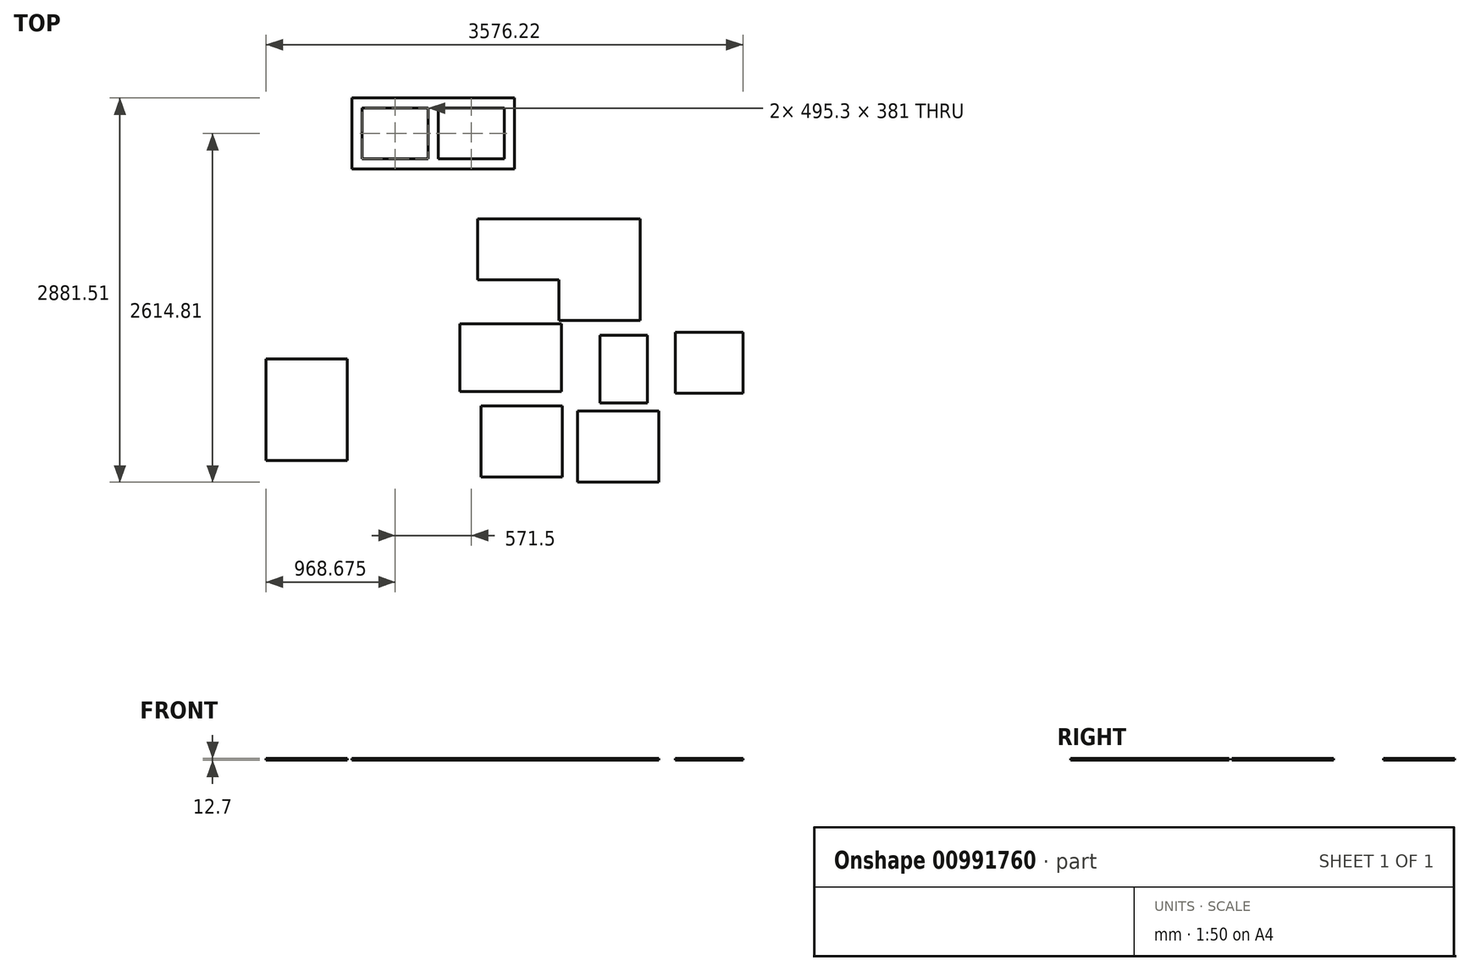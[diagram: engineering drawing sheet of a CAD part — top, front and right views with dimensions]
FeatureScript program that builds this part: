
annotation { "Feature Type Name" : "Feature", "Feature Type Description" : "" }
export const myFeature = defineFeature(function(context is Context, id is Id, definition is map)
    precondition{}
    {
        {
            var Q0;
            Q0=qCreatedBy(makeId("Top.planeOp"),FACE);
            var sketch = newSketch(context, id + "F0", { "sketchPlane" : qUnion([Q0])});
            skLineSegment(sketch, "E0.bottom", {"start": v(-682.65, 340.86) * mm, "end": v(536.55, 340.86) * mm});
            skLineSegment(sketch, "E0.top", {"start": v(-73.05, -421.14) * mm, "end": v(536.55, -421.14) * mm});
            skLineSegment(sketch, "E0.left", {"start": v(-682.65, 340.86) * mm, "end": v(-682.65, -116.34) * mm});
            skLineSegment(sketch, "E0.right", {"start": v(536.55, 340.86) * mm, "end": v(536.55, -421.14) * mm});
            skLineSegment(sketch, "E1", {"start": v(-682.65, -116.34) * mm, "end": v(-73.05, -116.34) * mm});
            skLineSegment(sketch, "E2", {"start": v(-73.05, -116.34) * mm, "end": v(-73.05, -421.14) * mm});
            skLineSegment(sketch, "E3.bottom", {"start": v(-815.3, -443.71) * mm, "end": v(-53.3, -443.71) * mm});
            skLineSegment(sketch, "E3.top", {"start": v(-815.3, -951.71) * mm, "end": v(-53.3, -951.71) * mm});
            skLineSegment(sketch, "E3.left", {"start": v(-815.3, -443.71) * mm, "end": v(-815.3, -951.71) * mm});
            skLineSegment(sketch, "E3.right", {"start": v(-53.3, -443.71) * mm, "end": v(-53.3, -951.71) * mm});
            skLineSegment(sketch, "E4.bottom", {"start": v(234.97, -530.08) * mm, "end": v(590.57, -530.08) * mm});
            skLineSegment(sketch, "E4.top", {"start": v(234.97, -1038.08) * mm, "end": v(590.57, -1038.08) * mm});
            skLineSegment(sketch, "E4.left", {"start": v(234.97, -530.08) * mm, "end": v(234.97, -1038.08) * mm});
            skLineSegment(sketch, "E4.right", {"start": v(590.57, -530.08) * mm, "end": v(590.57, -1038.08) * mm});
            skLineSegment(sketch, "E5.bottom", {"start": v(-656.38, -1060.91) * mm, "end": v(-46.78, -1060.91) * mm});
            skLineSegment(sketch, "E5.top", {"start": v(-656.38, -1594.31) * mm, "end": v(-46.78, -1594.31) * mm});
            skLineSegment(sketch, "E5.left", {"start": v(-656.38, -1060.91) * mm, "end": v(-656.38, -1594.31) * mm});
            skLineSegment(sketch, "E5.right", {"start": v(-46.78, -1060.91) * mm, "end": v(-46.78, -1594.31) * mm});
            skLineSegment(sketch, "E6.bottom", {"start": v(65.68, -1098.92) * mm, "end": v(675.28, -1098.92) * mm});
            skLineSegment(sketch, "E6.top", {"start": v(65.68, -1632.32) * mm, "end": v(675.28, -1632.32) * mm});
            skLineSegment(sketch, "E6.left", {"start": v(65.68, -1098.92) * mm, "end": v(65.68, -1632.32) * mm});
            skLineSegment(sketch, "E6.right", {"start": v(675.28, -1098.92) * mm, "end": v(675.28, -1632.32) * mm});
            skLineSegment(sketch, "E7.bottom", {"start": v(798.33, -507.17) * mm, "end": v(1306.33, -507.17) * mm});
            skLineSegment(sketch, "E7.top", {"start": v(798.33, -964.37) * mm, "end": v(1306.33, -964.37) * mm});
            skLineSegment(sketch, "E7.left", {"start": v(798.33, -507.17) * mm, "end": v(798.33, -964.37) * mm});
            skLineSegment(sketch, "E7.right", {"start": v(1306.33, -507.17) * mm, "end": v(1306.33, -964.37) * mm});
            skLineSegment(sketch, "E8.bottom", {"start": v(-2269.89, -710.02) * mm, "end": v(-1660.29, -710.02) * mm});
            skLineSegment(sketch, "E8.top", {"start": v(-2269.89, -1472.02) * mm, "end": v(-1660.29, -1472.02) * mm});
            skLineSegment(sketch, "E8.left", {"start": v(-2269.89, -710.02) * mm, "end": v(-2269.89, -1472.02) * mm});
            skLineSegment(sketch, "E8.right", {"start": v(-1660.29, -710.02) * mm, "end": v(-1660.29, -1472.02) * mm});
            skText(sketch, "E9", { "text": "X2", "fontName": "OpenSans-Regular.ttf"});
            skLineSegment(sketch, "E10.bottom", {"start": v(-1625.06, 1249.19) * mm, "end": v(-405.86, 1249.19) * mm});
            skLineSegment(sketch, "E10.top", {"start": v(-1625.06, 715.79) * mm, "end": v(-405.86, 715.79) * mm});
            skLineSegment(sketch, "E10.left", {"start": v(-1625.06, 1249.19) * mm, "end": v(-1625.06, 715.79) * mm});
            skLineSegment(sketch, "E10.right", {"start": v(-405.86, 1249.19) * mm, "end": v(-405.86, 715.79) * mm});
            skLineSegment(sketch, "E11.bottom", {"start": v(-1548.86, 1172.99) * mm, "end": v(-1053.56, 1172.99) * mm});
            skLineSegment(sketch, "E11.top", {"start": v(-1548.86, 791.99) * mm, "end": v(-1053.56, 791.99) * mm});
            skLineSegment(sketch, "E11.left", {"start": v(-1548.86, 1172.99) * mm, "end": v(-1548.86, 791.99) * mm});
            skLineSegment(sketch, "E11.right", {"start": v(-482.06, 1172.99) * mm, "end": v(-482.06, 791.99) * mm});
            skLineSegment(sketch, "E12", {"start": v(-1015.46, 1249.19) * mm, "end": v(-1015.46, 640.4) * mm, "construction": true});
            skLineSegment(sketch, "E13", {"start": v(-1053.56, 1172.99) * mm, "end": v(-1053.56, 791.99) * mm});
            skLineSegment(sketch, "E14", {"start": v(-977.36, 1172.99) * mm, "end": v(-977.36, 791.99) * mm});
            skLineSegment(sketch, "E15.trimOffspring", {"start": v(-977.36, 1172.99) * mm, "end": v(-482.06, 1172.99) * mm});
            skLineSegment(sketch, "E16.trimOffspring", {"start": v(-977.36, 791.99) * mm, "end": v(-482.06, 791.99) * mm});
            const initialGuessF0  = {"E9": [0.90316, 0.09607, 1, 0, 0.20292]};
            skSetInitialGuess(sketch, initialGuessF0);
            skSolve(sketch);
        }
        {
            var Q0;
            Q0=makeQuery(id+"F0.imprint","IMPRINT",FACE,{"disambiguationData":[TD([[makeQuery(id+"F0.imprint","IMPRINT",EDGE,{"derivedFrom":sQuery(id+"F0.wireOp",EDGE,"E0.bottom")}),-1.0]])]});
            var Q1;
            Q1=makeQuery(id+"F0.imprint","IMPRINT",FACE,{"disambiguationData":[TD([[makeQuery(id+"F0.imprint","IMPRINT",EDGE,{"derivedFrom":sQuery(id+"F0.wireOp",EDGE,"E3.bottom")}),-1.0]])]});
            var Q2;
            Q2=makeQuery(id+"F0.imprint","IMPRINT",FACE,{"disambiguationData":[TD([[makeQuery(id+"F0.imprint","IMPRINT",EDGE,{"derivedFrom":sQuery(id+"F0.wireOp",EDGE,"E5.bottom")}),-1.0]])]});
            var Q3;
            Q3=makeQuery(id+"F0.imprint","IMPRINT",FACE,{"disambiguationData":[TD([[makeQuery(id+"F0.imprint","IMPRINT",EDGE,{"derivedFrom":sQuery(id+"F0.wireOp",EDGE,"E6.bottom")}),-1.0]])]});
            var Q4;
            Q4=makeQuery(id+"F0.imprint","IMPRINT",FACE,{"disambiguationData":[TD([[makeQuery(id+"F0.imprint","IMPRINT",EDGE,{"derivedFrom":sQuery(id+"F0.wireOp",EDGE,"E4.bottom")}),-1.0]])]});
            var Q5;
            Q5=makeQuery(id+"F0.imprint","IMPRINT",FACE,{"disambiguationData":[TD([[makeQuery(id+"F0.imprint","IMPRINT",EDGE,{"derivedFrom":sQuery(id+"F0.wireOp",EDGE,"E7.bottom")}),-1.0]])]});
            var Q6;
            Q6=makeQuery(id+"F0.imprint","IMPRINT",FACE,{"disambiguationData":[TD([[makeQuery(id+"F0.imprint","IMPRINT",EDGE,{"derivedFrom":sQuery(id+"F0.wireOp",EDGE,"E8.bottom")}),-1.0]])]});
            var Q7;
            Q7=makeQuery(id+"F0.imprint","IMPRINT",FACE,{"disambiguationData":[TD([[makeQuery(id+"F0.imprint","IMPRINT",EDGE,{"derivedFrom":sQuery(id+"F0.wireOp",EDGE,"DP6RKWaR-zbFV-eJDy-ee4O-26oY3Mb155eF.bottom")}),-1.0]])]});
            var Q8;
            Q8=makeQuery(id+"F0.imprint","IMPRINT",FACE,{"disambiguationData":[TD([[makeQuery(id+"F0.imprint","IMPRINT",EDGE,{"derivedFrom":sQuery(id+"F0.wireOp",EDGE,"E10.bottom")}),-1.0]])]});
            extrude(context, id + "F1", {"entities" : qUnion([Q0, Q1, Q2, Q3, Q4, Q5, Q6, Q7, Q8]), "depth" : 12.7 * mm, "offsetDistance" : 25.4 * mm});
        }
    });
